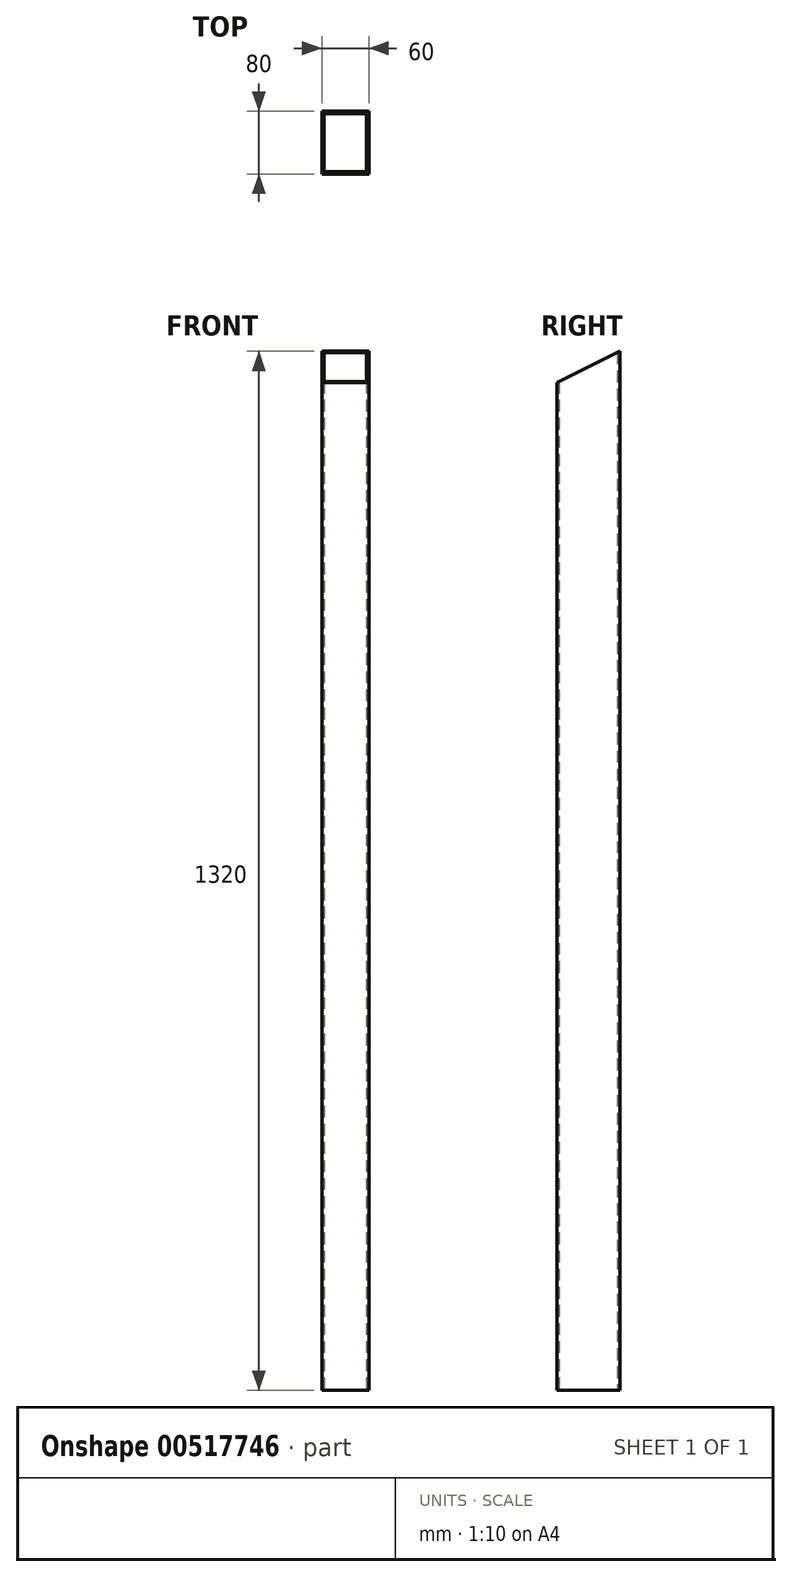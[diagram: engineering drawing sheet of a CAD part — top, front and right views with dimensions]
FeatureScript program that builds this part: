
annotation { "Feature Type Name" : "Feature", "Feature Type Description" : "" }
export const myFeature = defineFeature(function(context is Context, id is Id, definition is map)
    precondition{}
    {
        {
            var Q0;
            Q0=qCreatedBy(makeId("Right.planeOp"),FACE);
            var sketch = newSketch(context, id + "F0", { "sketchPlane" : qUnion([Q0])});
            skLineSegment(sketch, "E0", {"start": v(0, 0) * mm, "end": v(80, 0) * mm});
            skLineSegment(sketch, "E1", {"start": v(80, 0) * mm, "end": v(80, 1320) * mm});
            skLineSegment(sketch, "E2", {"start": v(80, 1320) * mm, "end": v(0, 1280) * mm});
            skLineSegment(sketch, "E3", {"start": v(0, 1280) * mm, "end": v(0, 0) * mm});
            skSolve(sketch);
        }
        {
            var Q0;
            Q0 = qSketchRegion(id + "F0", true);
            extrude(context, id + "F1", {"entities" : qUnion([Q0]), "depth" : 60 * mm, "offsetDistance" : 25 * mm});
        }
        {
            var Q0;
            Q0=makeQuery(id+"F1.opExtrude","SWEPT_FACE",FACE,{"disambiguationData":[OSD([sQuery(id+"F0.wireOp",EDGE,"E0")])]});
            var sketch = newSketch(context, id + "F2", { "sketchPlane" : qUnion([Q0])});
            skLineSegment(sketch, "E4.bottom", {"start": v(3, -3) * mm, "end": v(57, -3) * mm});
            skLineSegment(sketch, "E4.top", {"start": v(3, -77) * mm, "end": v(57, -77) * mm});
            skLineSegment(sketch, "E4.left", {"start": v(3, -3) * mm, "end": v(3, -77) * mm});
            skLineSegment(sketch, "E4.right", {"start": v(57, -3) * mm, "end": v(57, -77) * mm});
            skSolve(sketch);
        }
        {
            var Q0;
            Q0=makeQuery(id+"F2.imprint","IMPRINT",FACE,{"disambiguationData":[TD([[makeQuery(id+"F2.imprint","IMPRINT",EDGE,{"derivedFrom":sQuery(id+"F2.wireOp",EDGE,"E4.bottom")}),-1.0]])]});
            extrude(context, id + "F3", {"entities" : qUnion([Q0]), "operationType" : NewBodyOperationType.REMOVE, "endBound" : BoundingType.THROUGH_ALL, "oppositeDirection" : true, "depth" : 25 * mm, "offsetDistance" : 25 * mm});
        }
    });
